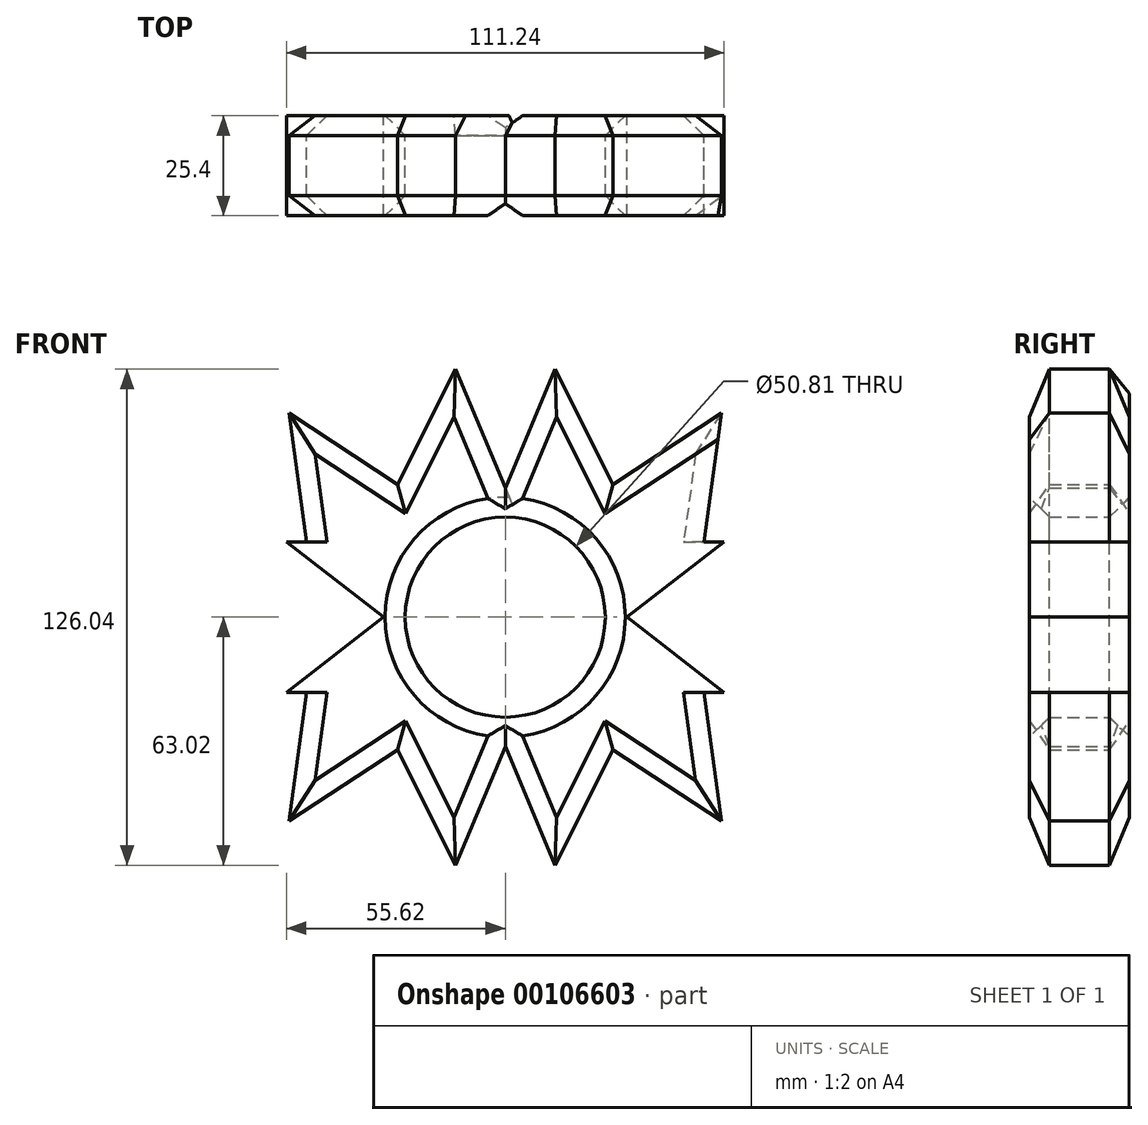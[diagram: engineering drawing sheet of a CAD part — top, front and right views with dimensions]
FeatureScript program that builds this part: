
annotation { "Feature Type Name" : "Feature", "Feature Type Description" : "" }
export const myFeature = defineFeature(function(context is Context, id is Id, definition is map)
    precondition{}
    {
        {
            var Q0;
            Q0=qCreatedBy(makeId("Front.planeOp"),FACE);
            var sketch = newSketch(context, id + "F0", { "sketchPlane" : qUnion([Q0])});
            skCircle(sketch, "E0", {"center": v(0, 0) * mm, "radius": 25.4 * mm});
            skLineSegment(sketch, "E1", {"start": v(-30.9, 0) * mm, "end": v(-50.42, 19.1) * mm});
            skLineSegment(sketch, "E2", {"start": v(-50.42, 19.1) * mm, "end": v(-27.33, 33.72) * mm});
            skLineSegment(sketch, "E3", {"start": v(-27.33, 33.72) * mm, "end": v(0, 32.79) * mm});
            skLineSegment(sketch, "E4.MirrorCS", {"start": v(27.33, 33.72) * mm, "end": v(0, 32.79) * mm});
            skLineSegment(sketch, "E5.MirrorCS", {"start": v(50.42, 19.1) * mm, "end": v(27.33, 33.72) * mm});
            skLineSegment(sketch, "E6.MirrorCS", {"start": v(30.9, 0) * mm, "end": v(50.42, 19.1) * mm});
            skLineSegment(sketch, "E7.MirrorCS", {"start": v(-27.33, -33.72) * mm, "end": v(0, -32.79) * mm});
            skLineSegment(sketch, "E8.MirrorCS", {"start": v(-50.42, -19.1) * mm, "end": v(-27.33, -33.72) * mm});
            skLineSegment(sketch, "E9.MirrorCS", {"start": v(-30.9, 0) * mm, "end": v(-50.42, -19.1) * mm});
            skLineSegment(sketch, "E10.MirrorCS", {"start": v(27.33, -33.72) * mm, "end": v(0, -32.79) * mm});
            skLineSegment(sketch, "E11.MirrorCS", {"start": v(50.42, -19.1) * mm, "end": v(27.33, -33.72) * mm});
            skLineSegment(sketch, "E12.MirrorCS", {"start": v(30.9, 0) * mm, "end": v(50.42, -19.1) * mm});
            skLineSegment(sketch, "E13", {"start": v(-50.42, 19.1) * mm, "end": v(-54.95, 51.82) * mm});
            skLineSegment(sketch, "E14", {"start": v(-54.95, 51.82) * mm, "end": v(-27.33, 33.72) * mm});
            skLineSegment(sketch, "E15", {"start": v(0, 32.79) * mm, "end": v(12.64, 63.02) * mm});
            skLineSegment(sketch, "E16", {"start": v(27.33, 33.72) * mm, "end": v(12.64, 63.02) * mm});
            skLineSegment(sketch, "E17.MirrorCS", {"start": v(54.95, 51.82) * mm, "end": v(27.33, 33.72) * mm});
            skLineSegment(sketch, "E18.MirrorCS", {"start": v(50.42, 19.1) * mm, "end": v(54.95, 51.82) * mm});
            skLineSegment(sketch, "E19.MirrorCS", {"start": v(-50.42, -19.1) * mm, "end": v(-54.95, -51.82) * mm});
            skLineSegment(sketch, "E20.MirrorCS", {"start": v(-54.95, -51.82) * mm, "end": v(-27.33, -33.72) * mm});
            skLineSegment(sketch, "E21.MirrorCS", {"start": v(0, -32.79) * mm, "end": v(12.64, -63.02) * mm});
            skLineSegment(sketch, "E22.MirrorCS", {"start": v(27.33, -33.72) * mm, "end": v(12.64, -63.02) * mm});
            skLineSegment(sketch, "E23.MirrorCS", {"start": v(54.95, -51.82) * mm, "end": v(27.33, -33.72) * mm});
            skLineSegment(sketch, "E24.MirrorCS", {"start": v(50.42, -19.1) * mm, "end": v(54.95, -51.82) * mm});
            skLineSegment(sketch, "E25", {"start": v(-50.42, 19.1) * mm, "end": v(-55.62, 19.1) * mm});
            skLineSegment(sketch, "E26", {"start": v(-55.62, 19.1) * mm, "end": v(-30.9, 0) * mm});
            skLineSegment(sketch, "E27.MirrorCS", {"start": v(50.42, 19.1) * mm, "end": v(55.62, 19.1) * mm});
            skLineSegment(sketch, "E28.MirrorCS", {"start": v(55.62, 19.1) * mm, "end": v(30.9, 0) * mm});
            skLineSegment(sketch, "E29.MirrorCS", {"start": v(-55.62, -19.1) * mm, "end": v(-30.9, 0) * mm});
            skLineSegment(sketch, "E30.MirrorCS", {"start": v(-50.42, -19.1) * mm, "end": v(-55.62, -19.1) * mm});
            skLineSegment(sketch, "E31.MirrorCS", {"start": v(50.42, -19.1) * mm, "end": v(55.62, -19.1) * mm});
            skLineSegment(sketch, "E32.MirrorCS", {"start": v(55.62, -19.1) * mm, "end": v(30.9, 0) * mm});
            skLineSegment(sketch, "E33.MirrorCS", {"start": v(-27.33, 33.72) * mm, "end": v(-12.64, 63.02) * mm});
            skLineSegment(sketch, "E34.MirrorCS", {"start": v(0, 32.79) * mm, "end": v(-12.64, 63.02) * mm});
            skLineSegment(sketch, "E35.MirrorCS", {"start": v(-27.33, -33.72) * mm, "end": v(-12.64, -63.02) * mm});
            skLineSegment(sketch, "E36.MirrorCS", {"start": v(0, -32.79) * mm, "end": v(-12.64, -63.02) * mm});
            skSolve(sketch);
        }
        {
            var Q0;
            Q0=makeQuery(id+"F0.imprint","IMPRINT",FACE,{"disambiguationData":[TD([[makeQuery(id+"F0.imprint","IMPRINT",EDGE,{"derivedFrom":sQuery(id+"F0.wireOp",EDGE,"E1")}),1.0]])]});
            var Q1;
            Q1=makeQuery(id+"F0.imprint","IMPRINT",FACE,{"disambiguationData":[TD([[makeQuery(id+"F0.imprint","IMPRINT",EDGE,{"derivedFrom":sQuery(id+"F0.wireOp",EDGE,"E2")}),1.0]])]});
            var Q2;
            Q2=makeQuery(id+"F0.imprint","IMPRINT",FACE,{"disambiguationData":[TD([[makeQuery(id+"F0.imprint","IMPRINT",EDGE,{"derivedFrom":sQuery(id+"F0.wireOp",EDGE,"E3")}),1.0]])]});
            var Q3;
            Q3=makeQuery(id+"F0.imprint","IMPRINT",FACE,{"disambiguationData":[TD([[makeQuery(id+"F0.imprint","IMPRINT",EDGE,{"derivedFrom":sQuery(id+"F0.wireOp",EDGE,"E4.MirrorCS")}),-1.0]])]});
            var Q4;
            Q4=makeQuery(id+"F0.imprint","IMPRINT",FACE,{"disambiguationData":[TD([[makeQuery(id+"F0.imprint","IMPRINT",EDGE,{"derivedFrom":sQuery(id+"F0.wireOp",EDGE,"E5.MirrorCS")}),-1.0]])]});
            var Q5;
            Q5=makeQuery(id+"F0.imprint","IMPRINT",FACE,{"disambiguationData":[TD([[makeQuery(id+"F0.imprint","IMPRINT",EDGE,{"derivedFrom":sQuery(id+"F0.wireOp",EDGE,"E6.MirrorCS")}),-1.0]])]});
            var Q6;
            Q6=makeQuery(id+"F0.imprint","IMPRINT",FACE,{"disambiguationData":[TD([[makeQuery(id+"F0.imprint","IMPRINT",EDGE,{"derivedFrom":sQuery(id+"F0.wireOp",EDGE,"E7.MirrorCS")}),-1.0]])]});
            var Q7;
            Q7=makeQuery(id+"F0.imprint","IMPRINT",FACE,{"disambiguationData":[TD([[makeQuery(id+"F0.imprint","IMPRINT",EDGE,{"derivedFrom":sQuery(id+"F0.wireOp",EDGE,"E8.MirrorCS")}),-1.0]])]});
            var Q8;
            Q8=makeQuery(id+"F0.imprint","IMPRINT",FACE,{"disambiguationData":[TD([[makeQuery(id+"F0.imprint","IMPRINT",EDGE,{"derivedFrom":sQuery(id+"F0.wireOp",EDGE,"E9.MirrorCS")}),-1.0]])]});
            var Q9;
            Q9=makeQuery(id+"F0.imprint","IMPRINT",FACE,{"disambiguationData":[TD([[makeQuery(id+"F0.imprint","IMPRINT",EDGE,{"derivedFrom":sQuery(id+"F0.wireOp",EDGE,"E10.MirrorCS")}),1.0]])]});
            var Q10;
            Q10=makeQuery(id+"F0.imprint","IMPRINT",FACE,{"disambiguationData":[TD([[makeQuery(id+"F0.imprint","IMPRINT",EDGE,{"derivedFrom":sQuery(id+"F0.wireOp",EDGE,"E11.MirrorCS")}),1.0]])]});
            var Q11;
            Q11=makeQuery(id+"F0.imprint","IMPRINT",FACE,{"disambiguationData":[TD([[makeQuery(id+"F0.imprint","IMPRINT",EDGE,{"derivedFrom":sQuery(id+"F0.wireOp",EDGE,"E12.MirrorCS")}),1.0]])]});
            var Q12;
            Q12=makeQuery(id+"F0.imprint","IMPRINT",FACE,{"disambiguationData":[TD([[makeQuery(id+"F0.imprint","IMPRINT",EDGE,{"derivedFrom":sQuery(id+"F0.wireOp",EDGE,"E0")}),-1.0]])]});
            extrude(context, id + "F1", {"entities" : qUnion([Q0, Q1, Q2, Q3, Q4, Q5, Q6, Q7, Q8, Q9, Q10, Q11, Q12]), "depth" : 25.4 * mm});
        }
        {
            var Q0;
            Q0=makeQuery(id+"F1.opExtrude","CAP_EDGE",EDGE,{"disambiguationData":[OSD([sQuery(id+"F0.wireOp",EDGE,"E0")])],"isStart":true});
            var Q1;
            Q1=makeQuery(id+"F1.opExtrude","CAP_EDGE",EDGE,{"disambiguationData":[OSD([sQuery(id+"F0.wireOp",EDGE,"E0")])],"isStart":false});
            chamfer(context, id + "F2", {"entities" : qUnion([Q0, Q1]), "width" : 5.08 * mm, "tangentPropagation" : true});
        }
        {
            var Q0;
            Q0=makeQuery(id+"F1.opExtrude","CAP_EDGE",EDGE,{"disambiguationData":[OSD([sQuery(id+"F0.wireOp",EDGE,"E33.MirrorCS")])],"isStart":true});
            var Q1;
            Q1=makeQuery(id+"F1.opExtrude","CAP_EDGE",EDGE,{"disambiguationData":[OSD([sQuery(id+"F0.wireOp",EDGE,"E14")])],"isStart":true});
            var Q2;
            Q2=makeQuery(id+"F1.opExtrude","CAP_EDGE",EDGE,{"disambiguationData":[OSD([sQuery(id+"F0.wireOp",EDGE,"E13")])],"isStart":true});
            var Q3;
            Q3=makeQuery(id+"F1.opExtrude","CAP_EDGE",EDGE,{"disambiguationData":[OSD([sQuery(id+"F0.wireOp",EDGE,"E19.MirrorCS")])],"isStart":true});
            var Q4;
            Q4=makeQuery(id+"F1.opExtrude","CAP_EDGE",EDGE,{"disambiguationData":[OSD([sQuery(id+"F0.wireOp",EDGE,"E20.MirrorCS")])],"isStart":true});
            var Q5;
            Q5=makeQuery(id+"F1.opExtrude","CAP_EDGE",EDGE,{"disambiguationData":[OSD([sQuery(id+"F0.wireOp",EDGE,"E35.MirrorCS")])],"isStart":true});
            var Q6;
            Q6=makeQuery(id+"F1.opExtrude","CAP_EDGE",EDGE,{"disambiguationData":[OSD([sQuery(id+"F0.wireOp",EDGE,"E36.MirrorCS")])],"isStart":true});
            var Q7;
            Q7=makeQuery(id+"F1.opExtrude","CAP_EDGE",EDGE,{"disambiguationData":[OSD([sQuery(id+"F0.wireOp",EDGE,"E21.MirrorCS")])],"isStart":true});
            var Q8;
            Q8=makeQuery(id+"F1.opExtrude","CAP_EDGE",EDGE,{"disambiguationData":[OSD([sQuery(id+"F0.wireOp",EDGE,"E22.MirrorCS")])],"isStart":true});
            var Q9;
            Q9=makeQuery(id+"F1.opExtrude","CAP_EDGE",EDGE,{"disambiguationData":[OSD([sQuery(id+"F0.wireOp",EDGE,"E23.MirrorCS")])],"isStart":true});
            var Q10;
            Q10=makeQuery(id+"F1.opExtrude","CAP_EDGE",EDGE,{"disambiguationData":[OSD([sQuery(id+"F0.wireOp",EDGE,"E24.MirrorCS")])],"isStart":true});
            var Q11;
            Q11=makeQuery(id+"F1.opExtrude","CAP_EDGE",EDGE,{"disambiguationData":[OSD([sQuery(id+"F0.wireOp",EDGE,"E15")])],"isStart":true});
            var Q12;
            Q12=makeQuery(id+"F1.opExtrude","CAP_EDGE",EDGE,{"disambiguationData":[OSD([sQuery(id+"F0.wireOp",EDGE,"E16")])],"isStart":true});
            var Q13;
            Q13=makeQuery(id+"F1.opExtrude","CAP_EDGE",EDGE,{"disambiguationData":[OSD([sQuery(id+"F0.wireOp",EDGE,"E17.MirrorCS")])],"isStart":true});
            var Q14;
            Q14=makeQuery(id+"F1.opExtrude","CAP_EDGE",EDGE,{"disambiguationData":[OSD([sQuery(id+"F0.wireOp",EDGE,"E18.MirrorCS")])],"isStart":true});
            var Q15;
            Q15=makeQuery(id+"F1.opExtrude","CAP_EDGE",EDGE,{"disambiguationData":[OSD([sQuery(id+"F0.wireOp",EDGE,"E13")])],"isStart":false});
            var Q16;
            Q16=makeQuery(id+"F1.opExtrude","CAP_EDGE",EDGE,{"disambiguationData":[OSD([sQuery(id+"F0.wireOp",EDGE,"E14")])],"isStart":false});
            var Q17;
            Q17=makeQuery(id+"F1.opExtrude","CAP_EDGE",EDGE,{"disambiguationData":[OSD([sQuery(id+"F0.wireOp",EDGE,"E33.MirrorCS")])],"isStart":false});
            var Q18;
            Q18=makeQuery(id+"F1.opExtrude","CAP_EDGE",EDGE,{"disambiguationData":[OSD([sQuery(id+"F0.wireOp",EDGE,"E34.MirrorCS")])],"isStart":false});
            var Q19;
            Q19=makeQuery(id+"F1.opExtrude","CAP_EDGE",EDGE,{"disambiguationData":[OSD([sQuery(id+"F0.wireOp",EDGE,"E15")])],"isStart":false});
            var Q20;
            Q20=makeQuery(id+"F1.opExtrude","CAP_EDGE",EDGE,{"disambiguationData":[OSD([sQuery(id+"F0.wireOp",EDGE,"E17.MirrorCS")])],"isStart":false});
            var Q21;
            Q21=makeQuery(id+"F1.opExtrude","CAP_EDGE",EDGE,{"disambiguationData":[OSD([sQuery(id+"F0.wireOp",EDGE,"E24.MirrorCS")])],"isStart":false});
            var Q22;
            Q22=makeQuery(id+"F1.opExtrude","CAP_EDGE",EDGE,{"disambiguationData":[OSD([sQuery(id+"F0.wireOp",EDGE,"E23.MirrorCS")])],"isStart":false});
            var Q23;
            Q23=makeQuery(id+"F1.opExtrude","CAP_EDGE",EDGE,{"disambiguationData":[OSD([sQuery(id+"F0.wireOp",EDGE,"E16")])],"isStart":false});
            var Q24;
            Q24=makeQuery(id+"F1.opExtrude","CAP_EDGE",EDGE,{"disambiguationData":[OSD([sQuery(id+"F0.wireOp",EDGE,"E19.MirrorCS")])],"isStart":false});
            var Q25;
            Q25=makeQuery(id+"F1.opExtrude","CAP_EDGE",EDGE,{"disambiguationData":[OSD([sQuery(id+"F0.wireOp",EDGE,"E20.MirrorCS")])],"isStart":false});
            var Q26;
            Q26=makeQuery(id+"F1.opExtrude","CAP_EDGE",EDGE,{"disambiguationData":[OSD([sQuery(id+"F0.wireOp",EDGE,"E35.MirrorCS")])],"isStart":false});
            var Q27;
            Q27=makeQuery(id+"F1.opExtrude","CAP_EDGE",EDGE,{"disambiguationData":[OSD([sQuery(id+"F0.wireOp",EDGE,"E21.MirrorCS")])],"isStart":false});
            var Q28;
            Q28=makeQuery(id+"F1.opExtrude","CAP_EDGE",EDGE,{"disambiguationData":[OSD([sQuery(id+"F0.wireOp",EDGE,"E22.MirrorCS")])],"isStart":false});
            var Q29;
            Q29=makeQuery(id+"F1.opExtrude","CAP_EDGE",EDGE,{"disambiguationData":[OSD([sQuery(id+"F0.wireOp",EDGE,"E36.MirrorCS")])],"isStart":false});
            chamfer(context, id + "F3", {"entities" : qUnion([Q0, Q1, Q2, Q3, Q4, Q5, Q6, Q7, Q8, Q9, Q10, Q11, Q12, Q13, Q14, Q15, Q16, Q17, Q18, Q19, Q20, Q21, Q22, Q23, Q24, Q25, Q26, Q27, Q28, Q29]), "width" : 5.08 * mm, "tangentPropagation" : true});
        }
    });
